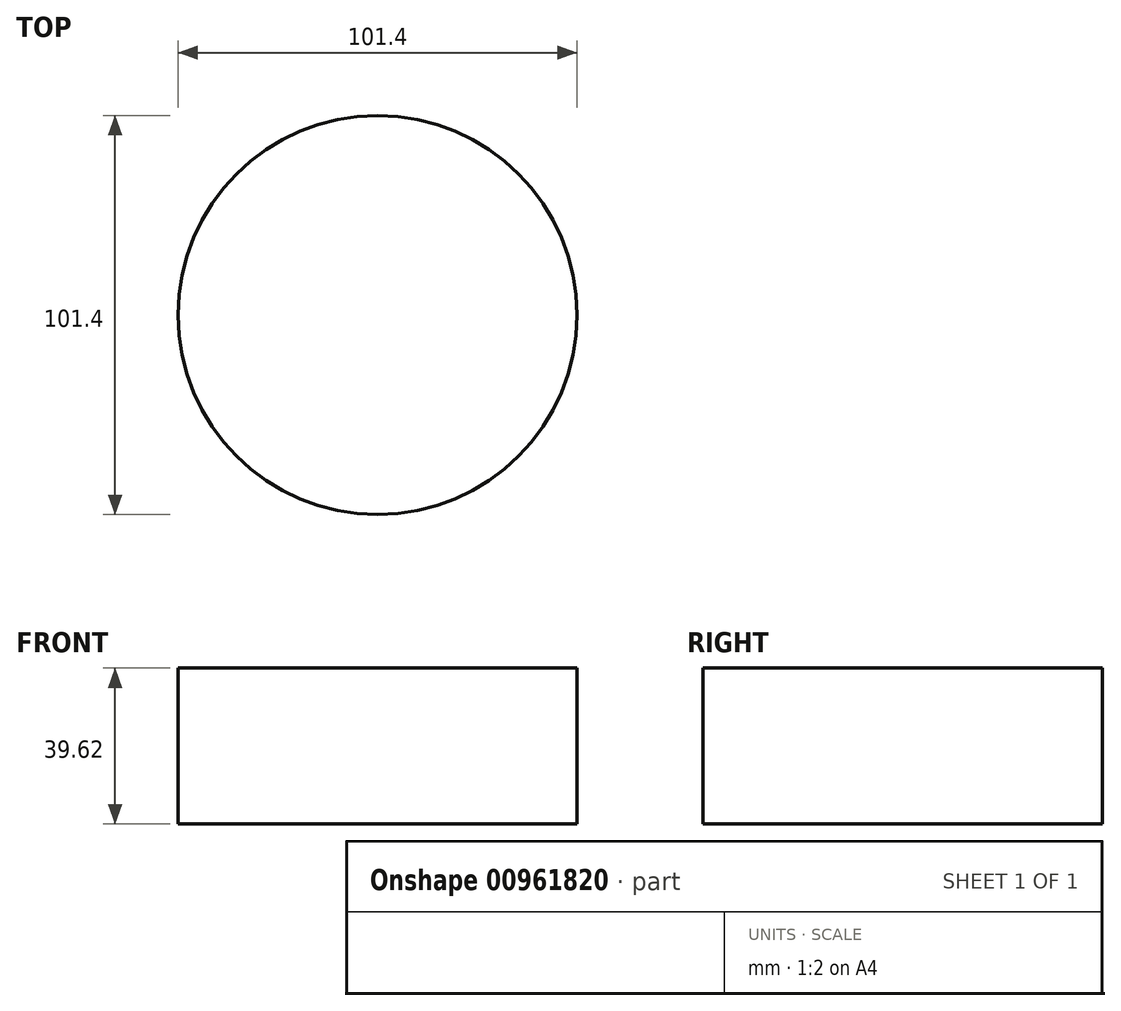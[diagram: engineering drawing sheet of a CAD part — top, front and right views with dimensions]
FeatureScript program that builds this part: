
annotation { "Feature Type Name" : "Feature", "Feature Type Description" : "" }
export const myFeature = defineFeature(function(context is Context, id is Id, definition is map)
    precondition{}
    {
        {
            var Q0;
            Q0=qCreatedBy(makeId("Top.planeOp"),FACE);
            var sketch = newSketch(context, id + "F0", { "sketchPlane" : qUnion([Q0])});
            skCircle(sketch, "E0", {"center": v(0, 0) * mm, "radius": 50.7 * mm});
            skSolve(sketch);
        }
        {
            var Q0;
            Q0 = qSketchRegion(id + "F0", true);
            extrude(context, id + "F1", {"entities" : qUnion([Q0]), "depth" : 39.62 * mm, "offsetDistance" : 25.4 * mm});
        }
    });
